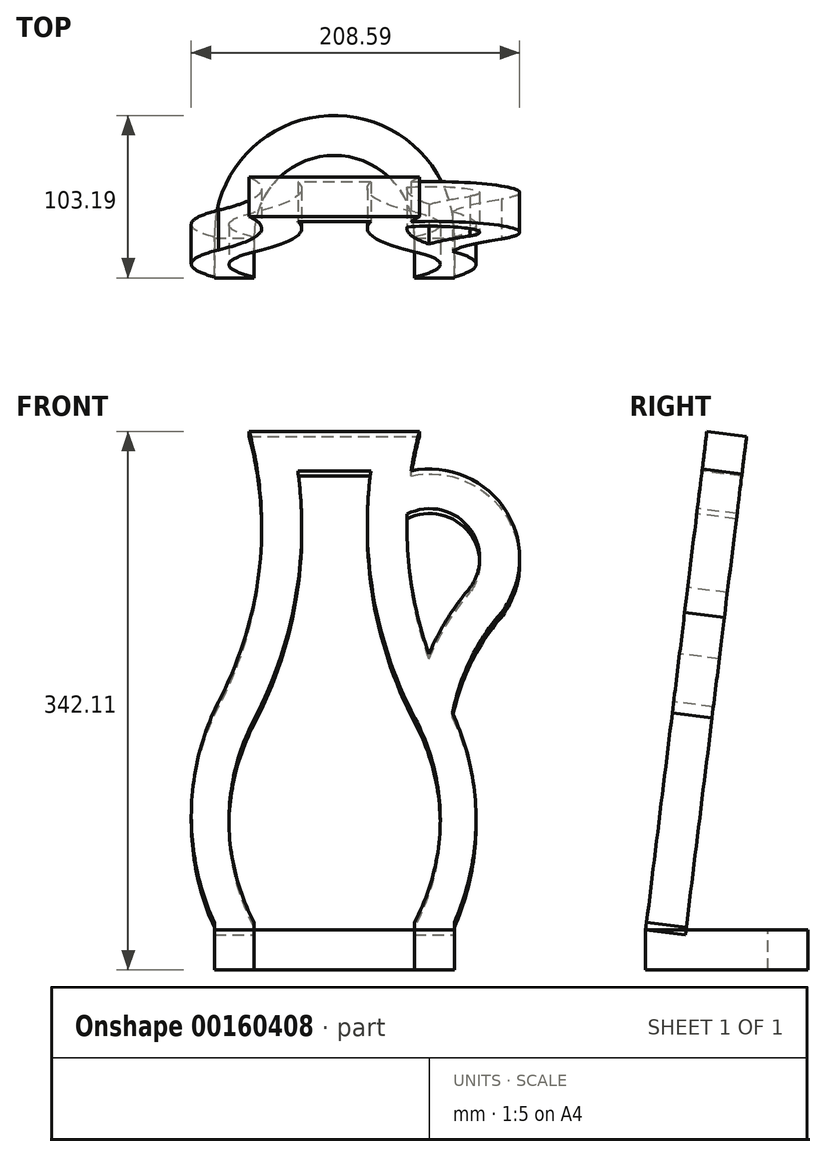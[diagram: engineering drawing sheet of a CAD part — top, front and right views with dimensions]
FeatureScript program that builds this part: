
annotation { "Feature Type Name" : "Feature", "Feature Type Description" : "" }
export const myFeature = defineFeature(function(context is Context, id is Id, definition is map)
    precondition{}
    {
        {
            var Q0;
            Q0=qCreatedBy(makeId("Top.planeOp"),FACE);
            var sketch = newSketch(context, id + "F0", { "sketchPlane" : qUnion([Q0])});
            skLineSegment(sketch, "E0", {"start": v(0, 0) * mm, "end": v(-62.54, 0) * mm});
            skSolve(sketch);
        }
        {
            var Q0;
            Q0=sQuery(id+"F0.wireOp",EDGE,"E0");
            var Q1;
            Q1=qCreatedBy(makeId("Front.planeOp"),FACE);
            cPlane(context, id + "F1", {"entities" : qUnion([Q0, Q1]), "cplaneType" : CPlaneType.LINE_ANGLE, "offset" : 25.4 * mm, "angle" : 7 * degree, "width" : 152.4 * mm, "height" : 152.4 * mm});
        }
        {
            var Q0;
            Q0=qCreatedBy(makeId("Top.planeOp"),FACE);
            cPlane(context, id + "F2", {"entities" : qUnion([Q0]), "cplaneType" : CPlaneType.OFFSET, "offset" : 0 * mm, "oppositeDirection" : true, "width" : 152.4 * mm, "height" : 152.4 * mm});
        }
        {
            var Q0;
            Q0=qCreatedBy(id+"F2.planeOp",FACE);
            var sketch = newSketch(context, id + "F3", { "sketchPlane" : qUnion([Q0])});
            skLineSegment(sketch, "E1", {"start": v(121.8, 0) * mm, "end": v(-111.18, 0) * mm, "construction": true});
            skLineSegment(sketch, "E2", {"start": v(0, 63.15) * mm, "end": v(0, -67.5) * mm, "construction": true});
            skLineSegment(sketch, "E3.bottom", {"start": v(-76.2, 0) * mm, "end": v(76.2, 0) * mm, "construction": true});
            skLineSegment(sketch, "E3.top", {"start": v(-76.2, 26.99) * mm, "end": v(76.2, 26.99) * mm, "construction": true});
            skLineSegment(sketch, "E3.left", {"start": v(-76.2, 0) * mm, "end": v(-76.2, 26.99) * mm});
            skLineSegment(sketch, "E3.right", {"start": v(76.2, 0) * mm, "end": v(76.2, 26.99) * mm});
            skPoint(sketch, "E4", {"position": v(0, 26.99) * mm});
            skLineSegment(sketch, "E5", {"start": v(-76.2, 0) * mm, "end": v(-50.8, 0) * mm});
            skLineSegment(sketch, "E6", {"start": v(-50.8, 0) * mm, "end": v(-50.8, 26.99) * mm});
            skLineSegment(sketch, "E7", {"start": v(76.2, 0) * mm, "end": v(50.8, 0) * mm});
            skLineSegment(sketch, "E8", {"start": v(50.8, 0) * mm, "end": v(50.8, 26.99) * mm});
            skArc(sketch, "E9", {"start": v(-50.8, 26.99) * mm, "mid": v(0, 77.79) * mm, "end": v(50.8, 26.99) * mm});
            skArc(sketch, "E10", {"start": v(-76.2, 26.99) * mm, "mid": v(0, 103.19) * mm, "end": v(76.2, 26.99) * mm});
            skSolve(sketch);
        }
        {
            var Q0;
            Q0 = qSketchRegion(id + "F3", true);
            extrude(context, id + "F4", {"entities" : qUnion([Q0]), "oppositeDirection" : true, "depth" : 25.4 * mm});
        }
        {
            var Q0;
            Q0=qCreatedBy(id+"F1.planeOp",FACE);
            var sketch = newSketch(context, id + "F5", { "sketchPlane" : qUnion([Q0])});
            skArc(sketch, "E11", {"start": v(-63.5, 4.76) * mm, "mid": v(-78.79, 73.23) * mm, "end": v(-61.79, 141.29) * mm, "construction": true});
            skArc(sketch, "E12", {"start": v(-61.79, 141.29) * mm, "mid": v(-36, 221.84) * mm, "end": v(-38.1, 306.39) * mm, "construction": true});
            skLineSegment(sketch, "E13", {"start": v(-38.1, 306.39) * mm, "end": v(0, 306.39) * mm, "construction": true});
            skArc(sketch, "E14", {"start": v(-33.98, 274.64) * mm, "mid": v(-92.13, 270.54) * mm, "end": v(-96.22, 212.4) * mm, "construction": true});
            skLineSegment(sketch, "E15", {"start": v(-33.98, 274.64) * mm, "end": v(-108.08, 200.54) * mm, "construction": true});
            skArc(sketch, "E16", {"start": v(-96.22, 212.4) * mm, "mid": v(-74.32, 179.11) * mm, "end": v(-61.79, 141.29) * mm, "construction": true});
            skLineSegment(sketch, "E17.MirrorCS", {"start": v(38.1, 306.39) * mm, "end": v(0, 306.39) * mm, "construction": true});
            skArc(sketch, "E18.MirrorCS", {"start": v(61.79, 141.29) * mm, "mid": v(36, 221.84) * mm, "end": v(38.1, 306.39) * mm, "construction": true});
            skArc(sketch, "E19.MirrorCS", {"start": v(63.5, 4.76) * mm, "mid": v(78.79, 73.23) * mm, "end": v(61.79, 141.29) * mm, "construction": true});
            skArc(sketch, "E20.0", {"start": v(-76.2, 4.76) * mm, "mid": v(-90.04, 71.91) * mm, "end": v(-75.1, 138.83) * mm});
            skArc(sketch, "E20.1", {"start": v(-60.2, 176.74) * mm, "mid": v(-49, 220.83) * mm, "end": v(-46.27, 266.24) * mm});
            skArc(sketch, "E20.2", {"start": v(76.2, 4.76) * mm, "mid": v(90.8, 75.66) * mm, "end": v(73.66, 145.99) * mm});
            skArc(sketch, "E20.3", {"start": v(73.66, 145.99) * mm, "mid": v(47.67, 230.7) * mm, "end": v(54.02, 319.09) * mm});
            skLineSegment(sketch, "E20.4", {"start": v(54.02, 319.09) * mm, "end": v(0, 319.09) * mm});
            skLineSegment(sketch, "E20.5", {"start": v(-54.02, 319.09) * mm, "end": v(0, 319.09) * mm});
            skArc(sketch, "E21.0", {"start": v(-50.8, 4.76) * mm, "mid": v(-67.3, 70) * mm, "end": v(-51.38, 135.4) * mm});
            skArc(sketch, "E21.1", {"start": v(-51.38, 135.4) * mm, "mid": v(-25.09, 212.37) * mm, "end": v(-23.21, 293.69) * mm});
            skArc(sketch, "E21.2", {"start": v(50.8, 4.76) * mm, "mid": v(66.87, 69.44) * mm, "end": v(51.16, 134.2) * mm});
            skArc(sketch, "E21.3", {"start": v(51.16, 134.2) * mm, "mid": v(24.75, 211.77) * mm, "end": v(23.14, 293.69) * mm});
            skLineSegment(sketch, "E21.4", {"start": v(23.14, 293.69) * mm, "end": v(0, 293.69) * mm});
            skLineSegment(sketch, "E21.5", {"start": v(-23.21, 293.69) * mm, "end": v(0, 293.69) * mm});
            skArc(sketch, "E22.0", {"start": v(-106.05, 203.24) * mm, "mid": v(-86.38, 173.05) * mm, "end": v(-75.1, 138.83) * mm});
            skArc(sketch, "E23.0", {"start": v(-86.2, 219.1) * mm, "mid": v(-71.6, 198.91) * mm, "end": v(-60.2, 176.74) * mm});
            skArc(sketch, "E24.trimOffspring", {"start": v(-48.82, 293.84) * mm, "mid": v(-108.94, 268.44) * mm, "end": v(-106.05, 203.24) * mm});
            skArc(sketch, "E25.trimOffspring", {"start": v(-48.82, 293.84) * mm, "mid": v(-51.08, 306.53) * mm, "end": v(-54.02, 319.09) * mm});
            skArc(sketch, "E26.trimOffspring", {"start": v(-46.27, 266.24) * mm, "mid": v(-84.85, 258.44) * mm, "end": v(-86.2, 219.1) * mm});
            skLineSegment(sketch, "E27.bottom", {"start": v(76.2, 0) * mm, "end": v(50.8, 0) * mm});
            skLineSegment(sketch, "E27.top", {"start": v(76.2, 4.76) * mm, "end": v(50.8, 4.76) * mm, "construction": true});
            skLineSegment(sketch, "E27.left", {"start": v(76.2, 0) * mm, "end": v(76.2, 4.76) * mm});
            skLineSegment(sketch, "E27.right", {"start": v(50.8, 0) * mm, "end": v(50.8, 4.76) * mm});
            skLineSegment(sketch, "E28.bottom", {"start": v(-50.8, 0) * mm, "end": v(-76.2, 0) * mm});
            skLineSegment(sketch, "E28.top", {"start": v(-50.8, 4.76) * mm, "end": v(-76.2, 4.76) * mm, "construction": true});
            skLineSegment(sketch, "E28.left", {"start": v(-50.8, 0) * mm, "end": v(-50.8, 4.76) * mm});
            skLineSegment(sketch, "E28.right", {"start": v(-76.2, 0) * mm, "end": v(-76.2, 4.76) * mm});
            skPoint(sketch, "E29", {"position": v(-63.5, 4.76) * mm});
            skPoint(sketch, "E30", {"position": v(63.5, 4.76) * mm});
            skSolve(sketch);
        }
        {
            var Q0;
            Q0 = qSketchRegion(id + "F5", true);
            extrude(context, id + "F6", {"entities" : qUnion([Q0]), "depth" : 25.4 * mm});
        }
    });
